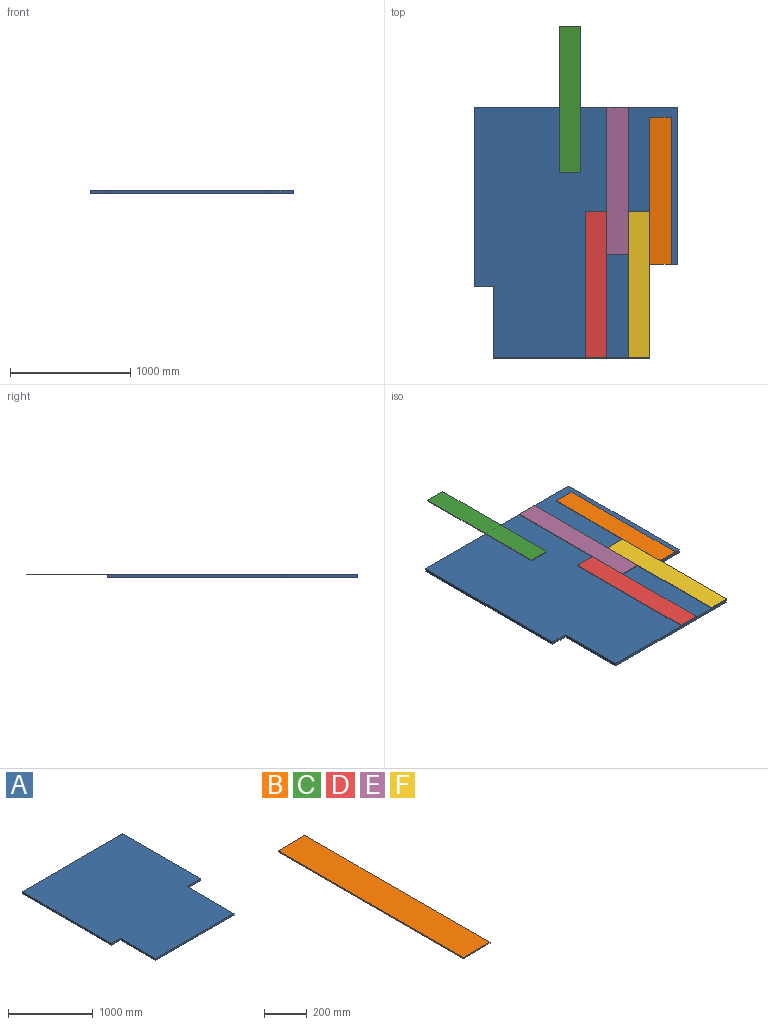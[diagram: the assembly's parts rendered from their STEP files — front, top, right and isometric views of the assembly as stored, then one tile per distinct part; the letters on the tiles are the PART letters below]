
ASSEMBLY  parts=6 mates=14
PART A: 10 faces, bbox 1682.8x2082.8x25.4 mm
  f0: plane 1682.75x25.4mm, normal (0,1,0), area 42741.8mm2, adj f1,f7,f8,f9
  f1: plane 1492.25x25.4mm, normal (-1,0,0), area 37903.1mm2, adj f0,f2,f8,f9
  f2: plane 152.4x25.4mm, normal (0,-1,0), area 3871mm2, adj f1,f3,f8,f9
  f3: plane 590.55x25.4mm, normal (-1,0,0), area 15000mm2, adj f2,f4,f8,f9
  f4: plane 1301.75x25.4mm, normal (0,-1,0), area 33064.4mm2, adj f3,f5,f8,f9
  f5: plane 781.05x25.4mm, normal (1,0,0), area 19838.7mm2, adj f4,f6,f8,f9
  f6: plane 228.6x25.4mm, normal (0,-1,0), area 5806.4mm2, adj f5,f7,f8,f9
  f7: plane 1301.75x25.4mm, normal (1,0,0), area 33064.5mm2, adj f0,f6,f8,f9
  f8: plane 2082.8x1682.75mm, normal (0,0,1), area 3236283.8mm2, adj f0,f1,f2,f3,f4,f5,f6,f7
  f9: plane 2082.8x1682.75mm, normal (0,0,-1), area 3236283.8mm2, adj f0,f1,f2,f3,f4,f5,f6,f7
PART B: 6 faces, bbox 177.8x1219.2x6.4 mm
  f0: plane 177.8x6.35mm, normal (0,1,0), area 1129mm2, adj f1,f3,f4,f5
  f1: plane 1219.2x6.35mm, normal (-1,0,0), area 7741.9mm2, adj f0,f2,f4,f5
  f2: plane 177.8x6.35mm, normal (0,-1,0), area 1129mm2, adj f1,f3,f4,f5
  f3: plane 1219.2x6.35mm, normal (1,0,0), area 7741.9mm2, adj f0,f2,f4,f5
  f4: plane 1219.2x177.8mm, normal (0,0,1), area 216773.8mm2, adj f0,f1,f2,f3
  f5: plane 1219.2x177.8mm, normal (0,0,-1), area 216773.8mm2, adj f0,f1,f2,f3
PART C: same geometry as B
PART D: same geometry as B
PART E: same geometry as B
PART F: same geometry as B
PLACE A t=(2260.91,5461.67,51.68)mm
PLACE B t=(3280.45,4668.13,77.08)mm
PLACE C t=(2528.8,5427.04,77.08)mm
PLACE D t=(2747.05,3887.08,77.08)mm
PLACE E t=(2924.85,4750.68,77.08)mm
PLACE F t=(3102.65,3887.08,77.08)mm
MATE planar C.f4 <-> E.f4  axis (0,0,1) through (2346.06,5427.12,83.43)mm
MATE planar E.f3 <-> F.f1  axis (1,0,0) through (2831.01,4750.76,80.25)mm
MATE planar E.f1 <-> D.f3  axis (-1,0,0) through (2653.21,4750.76,80.25)mm
MATE planar D.f2 <-> A.f4  axis (0,-1,0) through (2564.31,3277.56,80.25)mm
MATE planar E.f0 <-> A.f0  axis (0,1,0) through (2742.11,5360.36,80.25)mm
MATE planar F.f3 <-> A.f5  axis (1,0,0) through (3008.81,3887.16,80.25)mm
MATE planar F.f2 <-> A.f4  axis (0,-1,0) through (2919.91,3277.56,80.25)mm
MATE planar A.f8 <-> F.f5  axis (0,0,1) through (2377.2,4375.62,77.08)mm
MATE planar A.f6 <-> B.f2  axis (0,-1,0) through (3123.11,4058.61,64.38)mm
MATE planar C.f4 <-> E.f4  axis (0,0,1) through (2346.06,5427.12,83.43)mm
MATE planar F.f4 <-> B.f4  axis (0,0,1) through (2919.91,3887.16,83.43)mm
MATE planar F.f3 <-> B.f1  axis (1,0,0) through (3008.81,3887.16,80.25)mm
MATE planar E.f5 <-> A.f8  axis (0,0,-1) through (2742.11,4750.76,77.08)mm
MATE planar A.f8 <-> D.f5  axis (0,0,1) through (2377.2,4375.62,77.08)mm
